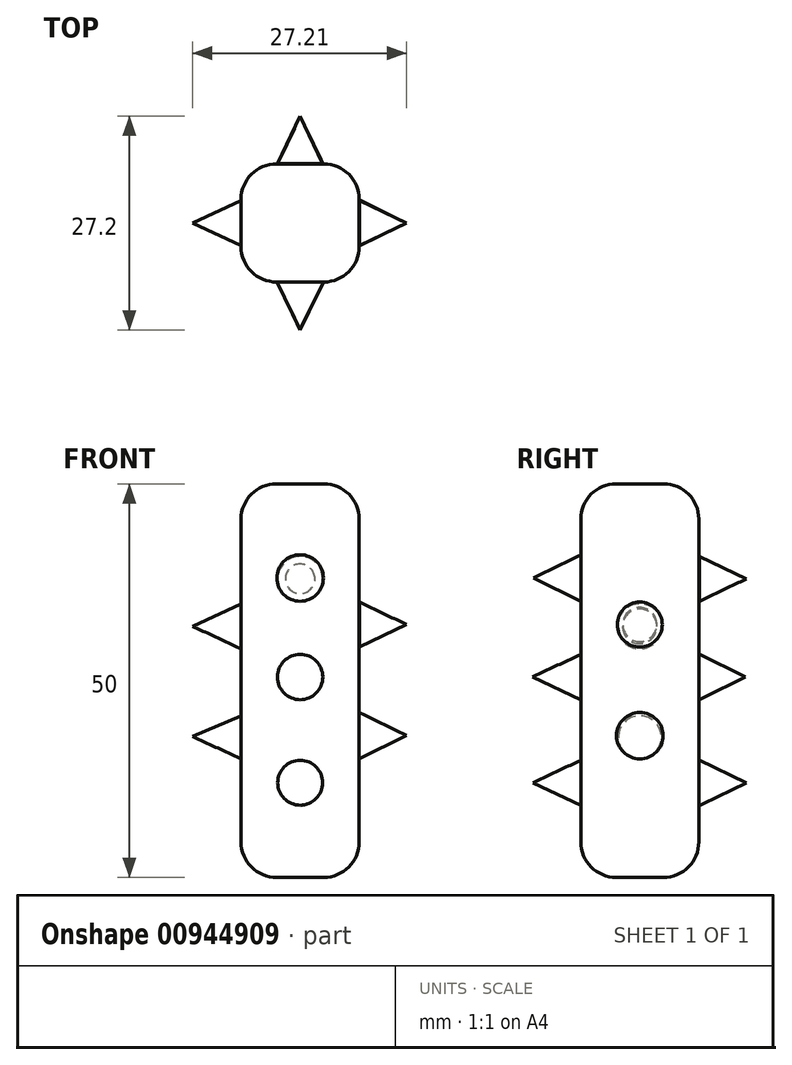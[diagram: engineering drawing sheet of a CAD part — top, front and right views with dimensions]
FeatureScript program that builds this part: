
annotation { "Feature Type Name" : "Feature", "Feature Type Description" : "" }
export const myFeature = defineFeature(function(context is Context, id is Id, definition is map)
    precondition{}
    {
        {
            var Q0;
            Q0=qCreatedBy(makeId("Top.planeOp"),FACE);
            var sketch = newSketch(context, id + "F0", { "sketchPlane" : qUnion([Q0])});
            skLineSegment(sketch, "E0.bottom", {"start": v(7.5, 7.5) * mm, "end": v(-7.5, 7.5) * mm});
            skLineSegment(sketch, "E0.top", {"start": v(7.5, -7.5) * mm, "end": v(-7.5, -7.5) * mm});
            skLineSegment(sketch, "E0.left", {"start": v(7.5, 7.5) * mm, "end": v(7.5, -7.5) * mm});
            skLineSegment(sketch, "E0.right", {"start": v(-7.5, 7.5) * mm, "end": v(-7.5, -7.5) * mm});
            skPoint(sketch, "E0.middle", {"position": v(0, 0) * mm});
            skSolve(sketch);
        }
        {
            var Q0;
            Q0=qSketchRegion(id+"F0",true);
            var Q1;
            Q1=makeQuery(id+"F0.imprint","IMPRINT",FACE,{"disambiguationData":[TD([[makeQuery(id+"F0.imprint","IMPRINT",EDGE,{"derivedFrom":sQuery(id+"F0.wireOp",EDGE,"E0.bottom")}),1.0]])]});
            extrude(context, id + "F1", {"entities" : qUnion([Q0, Q1]), "depth" : 50 * mm, "offsetDistance" : 25 * mm});
        }
        {
            var Q0;
            Q0=makeQuery(id+"F1.opExtrude","SWEPT_FACE",FACE,{"disambiguationData":[OSD([sQuery(id+"F0.wireOp",EDGE,"E0.left")])]});
            var Q1;
            Q1=makeQuery(id+"F1.opExtrude","SWEPT_FACE",FACE,{"disambiguationData":[OSD([sQuery(id+"F0.wireOp",EDGE,"E0.top")])]});
            var Q2;
            Q2=makeQuery(id+"F1.opExtrude","SWEPT_FACE",FACE,{"disambiguationData":[OSD([sQuery(id+"F0.wireOp",EDGE,"E0.right")])]});
            var Q3;
            Q3=makeQuery(id+"F1.opExtrude","SWEPT_FACE",FACE,{"disambiguationData":[OSD([sQuery(id+"F0.wireOp",EDGE,"E0.bottom")])]});
            fillet(context, id + "F2", {"entities" : qUnion([Q0, Q1, Q2, Q3]), "radius" : 4.5 * mm, "tangentPropagation" : true, "allowEdgeOverflow" : false});
        }
        {
            var Q0;
            Q0=qCreatedBy(makeId("Right.planeOp"),FACE);
            var sketch = newSketch(context, id + "F3", { "sketchPlane" : qUnion([Q0])});
            skLineSegment(sketch, "E1", {"start": v(-7.45, 38.03) * mm, "end": v(-13.53, 38.03) * mm});
            skLineSegment(sketch, "E2", {"start": v(-13.53, 38.03) * mm, "end": v(-7.48, 35.07) * mm});
            skLineSegment(sketch, "E3", {"start": v(-7.48, 35.07) * mm, "end": v(-7.45, 38.03) * mm});
            skLineSegment(sketch, "E4", {"start": v(-7.48, 25.45) * mm, "end": v(-13.63, 25.45) * mm});
            skLineSegment(sketch, "E5", {"start": v(-13.63, 25.45) * mm, "end": v(-7.45, 22.55) * mm});
            skLineSegment(sketch, "E6", {"start": v(-7.45, 22.55) * mm, "end": v(-7.48, 25.45) * mm});
            skLineSegment(sketch, "E7", {"start": v(-7.45, 12.02) * mm, "end": v(-13.6, 12.02) * mm});
            skLineSegment(sketch, "E8", {"start": v(-13.6, 12.02) * mm, "end": v(-7.45, 9.15) * mm});
            skLineSegment(sketch, "E9", {"start": v(-7.45, 9.15) * mm, "end": v(-7.45, 12.02) * mm});
            skSolve(sketch);
        }
        {
            var Q0;
            Q0=makeQuery(id+"F3.imprint","IMPRINT",FACE,{"disambiguationData":[TD([[makeQuery(id+"F3.imprint","IMPRINT",EDGE,{"derivedFrom":sQuery(id+"F3.wireOp",EDGE,"E1")}),1.0]])]});
            var Q1;
            Q1=sQuery(id+"F3.wireOp",EDGE,"E1");
            revolve(context, id + "F4", {"operationType" : NewBodyOperationType.ADD, "surfaceOperationType" : NewSurfaceOperationType.NEW, "entities" : qUnion([Q0]), "axis" : qUnion([Q1]), "revolveType" : RevolveType.FULL});
        }
        {
            var Q0;
            Q0=makeQuery(id+"F3.imprint","IMPRINT",FACE,{"disambiguationData":[TD([[makeQuery(id+"F3.imprint","IMPRINT",EDGE,{"derivedFrom":sQuery(id+"F3.wireOp",EDGE,"E4")}),1.0]])]});
            var Q1;
            Q1=sQuery(id+"F3.wireOp",EDGE,"E4");
            revolve(context, id + "F5", {"operationType" : NewBodyOperationType.ADD, "surfaceOperationType" : NewSurfaceOperationType.NEW, "entities" : qUnion([Q0]), "axis" : qUnion([Q1]), "revolveType" : RevolveType.FULL});
        }
        {
            var Q0;
            Q0=makeQuery(id+"F3.imprint","IMPRINT",FACE,{"disambiguationData":[TD([[makeQuery(id+"F3.imprint","IMPRINT",EDGE,{"derivedFrom":sQuery(id+"F3.wireOp",EDGE,"E7")}),1.0]])]});
            var Q1;
            Q1=sQuery(id+"F3.wireOp",EDGE,"E7");
            revolve(context, id + "F6", {"operationType" : NewBodyOperationType.ADD, "surfaceOperationType" : NewSurfaceOperationType.NEW, "entities" : qUnion([Q0]), "axis" : qUnion([Q1]), "revolveType" : RevolveType.FULL});
        }
        {
            var Q0;
            Q0=qCreatedBy(makeId("Right.planeOp"),FACE);
            var sketch = newSketch(context, id + "F7", { "sketchPlane" : qUnion([Q0])});
            skLineSegment(sketch, "E10", {"start": v(7.4, 37.93) * mm, "end": v(13.57, 37.93) * mm});
            skLineSegment(sketch, "E11", {"start": v(13.57, 37.93) * mm, "end": v(7.55, 35.08) * mm});
            skLineSegment(sketch, "E12", {"start": v(7.55, 35.08) * mm, "end": v(7.4, 37.93) * mm});
            skLineSegment(sketch, "E13", {"start": v(7.4, 25.45) * mm, "end": v(13.42, 25.45) * mm});
            skLineSegment(sketch, "E14", {"start": v(13.42, 25.45) * mm, "end": v(7.4, 22.48) * mm});
            skLineSegment(sketch, "E15", {"start": v(7.4, 22.48) * mm, "end": v(7.4, 25.45) * mm});
            skLineSegment(sketch, "E16", {"start": v(7.4, 12) * mm, "end": v(13.54, 12) * mm});
            skLineSegment(sketch, "E17", {"start": v(13.54, 12) * mm, "end": v(7.4, 9.04) * mm});
            skLineSegment(sketch, "E18", {"start": v(7.4, 9.04) * mm, "end": v(7.4, 12) * mm});
            skSolve(sketch);
        }
        {
            var Q0;
            Q0=makeQuery(id+"F7.imprint","IMPRINT",FACE,{"disambiguationData":[TD([[makeQuery(id+"F7.imprint","IMPRINT",EDGE,{"derivedFrom":sQuery(id+"F7.wireOp",EDGE,"E10")}),-1.0]])]});
            var Q1;
            Q1=sQuery(id+"F7.wireOp",EDGE,"E10");
            revolve(context, id + "F8", {"operationType" : NewBodyOperationType.ADD, "surfaceOperationType" : NewSurfaceOperationType.NEW, "entities" : qUnion([Q0]), "axis" : qUnion([Q1]), "revolveType" : RevolveType.FULL});
        }
        {
            var Q0;
            Q0=makeQuery(id+"F7.imprint","IMPRINT",FACE,{"disambiguationData":[TD([[makeQuery(id+"F7.imprint","IMPRINT",EDGE,{"derivedFrom":sQuery(id+"F7.wireOp",EDGE,"E13")}),-1.0]])]});
            var Q1;
            Q1=sQuery(id+"F7.wireOp",EDGE,"E13");
            revolve(context, id + "F9", {"operationType" : NewBodyOperationType.ADD, "surfaceOperationType" : NewSurfaceOperationType.NEW, "entities" : qUnion([Q0]), "axis" : qUnion([Q1]), "revolveType" : RevolveType.FULL});
        }
        {
            var Q0;
            Q0=makeQuery(id+"F7.imprint","IMPRINT",FACE,{"disambiguationData":[TD([[makeQuery(id+"F7.imprint","IMPRINT",EDGE,{"derivedFrom":sQuery(id+"F7.wireOp",EDGE,"E16")}),-1.0]])]});
            var Q1;
            Q1=sQuery(id+"F7.wireOp",EDGE,"E16");
            revolve(context, id + "F10", {"operationType" : NewBodyOperationType.ADD, "surfaceOperationType" : NewSurfaceOperationType.NEW, "entities" : qUnion([Q0]), "axis" : qUnion([Q1]), "revolveType" : RevolveType.FULL});
        }
        {
            var Q0;
            Q0=qCreatedBy(makeId("Front.planeOp"),FACE);
            var sketch = newSketch(context, id + "F11", { "sketchPlane" : qUnion([Q0])});
            skLineSegment(sketch, "E19", {"start": v(7.38, 32.12) * mm, "end": v(13.52, 32.12) * mm});
            skLineSegment(sketch, "E20", {"start": v(13.52, 32.12) * mm, "end": v(7.54, 29.26) * mm});
            skLineSegment(sketch, "E21", {"start": v(7.54, 29.26) * mm, "end": v(7.38, 32.12) * mm});
            skLineSegment(sketch, "E22", {"start": v(7.38, 18) * mm, "end": v(13.5, 18) * mm});
            skLineSegment(sketch, "E23", {"start": v(13.5, 18) * mm, "end": v(7.38, 14.99) * mm});
            skLineSegment(sketch, "E24", {"start": v(7.38, 14.99) * mm, "end": v(7.38, 18) * mm});
            skSolve(sketch);
        }
        {
            var Q0;
            Q0=makeQuery(id+"F11.imprint","IMPRINT",FACE,{"disambiguationData":[TD([[makeQuery(id+"F11.imprint","IMPRINT",EDGE,{"derivedFrom":sQuery(id+"F11.wireOp",EDGE,"E19")}),-1.0]])]});
            var Q1;
            Q1=sQuery(id+"F11.wireOp",EDGE,"E19");
            revolve(context, id + "F12", {"operationType" : NewBodyOperationType.ADD, "surfaceOperationType" : NewSurfaceOperationType.NEW, "entities" : qUnion([Q0]), "axis" : qUnion([Q1]), "revolveType" : RevolveType.FULL});
        }
        {
            var Q0;
            Q0=makeQuery(id+"F11.imprint","IMPRINT",FACE,{"disambiguationData":[TD([[makeQuery(id+"F11.imprint","IMPRINT",EDGE,{"derivedFrom":sQuery(id+"F11.wireOp",EDGE,"E22")}),-1.0]])]});
            var Q1;
            Q1=sQuery(id+"F11.wireOp",EDGE,"E22");
            revolve(context, id + "F13", {"operationType" : NewBodyOperationType.ADD, "surfaceOperationType" : NewSurfaceOperationType.NEW, "entities" : qUnion([Q0]), "axis" : qUnion([Q1]), "revolveType" : RevolveType.FULL});
        }
        {
            var Q0;
            Q0=qCreatedBy(makeId("Front.planeOp"),FACE);
            var sketch = newSketch(context, id + "F14", { "sketchPlane" : qUnion([Q0])});
            skLineSegment(sketch, "E25", {"start": v(-7.46, 31.9) * mm, "end": v(-13.65, 31.9) * mm});
            skLineSegment(sketch, "E26", {"start": v(-13.65, 31.9) * mm, "end": v(-7.51, 29.03) * mm});
            skLineSegment(sketch, "E27", {"start": v(-7.51, 29.03) * mm, "end": v(-7.46, 31.9) * mm});
            skLineSegment(sketch, "E28", {"start": v(-7.46, 17.8) * mm, "end": v(-13.69, 17.92) * mm});
            skLineSegment(sketch, "E29", {"start": v(-13.69, 17.92) * mm, "end": v(-7.46, 15.02) * mm});
            skLineSegment(sketch, "E30", {"start": v(-7.46, 15.02) * mm, "end": v(-7.46, 17.8) * mm});
            skSolve(sketch);
        }
        {
            var Q0;
            Q0=makeQuery(id+"F14.imprint","IMPRINT",FACE,{"disambiguationData":[TD([[makeQuery(id+"F14.imprint","IMPRINT",EDGE,{"derivedFrom":sQuery(id+"F14.wireOp",EDGE,"E25")}),1.0]])]});
            var Q1;
            Q1=sQuery(id+"F14.wireOp",EDGE,"E25");
            revolve(context, id + "F15", {"operationType" : NewBodyOperationType.ADD, "surfaceOperationType" : NewSurfaceOperationType.NEW, "entities" : qUnion([Q0]), "axis" : qUnion([Q1]), "revolveType" : RevolveType.FULL});
        }
        {
            var Q0;
            Q0=makeQuery(id+"F14.imprint","IMPRINT",FACE,{"disambiguationData":[TD([[makeQuery(id+"F14.imprint","IMPRINT",EDGE,{"derivedFrom":sQuery(id+"F14.wireOp",EDGE,"E28")}),1.0]])]});
            var Q1;
            Q1=sQuery(id+"F14.wireOp",EDGE,"E28");
            revolve(context, id + "F16", {"operationType" : NewBodyOperationType.ADD, "surfaceOperationType" : NewSurfaceOperationType.NEW, "entities" : qUnion([Q0]), "axis" : qUnion([Q1]), "revolveType" : RevolveType.FULL});
        }
    });
